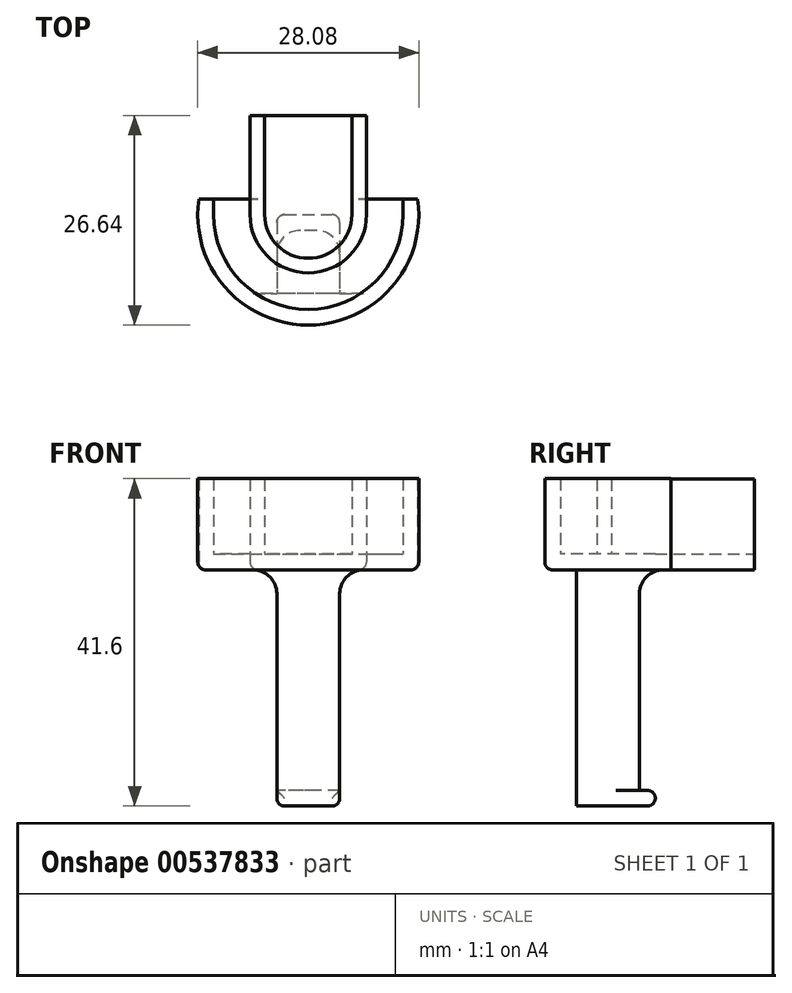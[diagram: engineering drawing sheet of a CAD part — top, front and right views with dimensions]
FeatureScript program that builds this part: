
annotation { "Feature Type Name" : "Feature", "Feature Type Description" : "" }
export const myFeature = defineFeature(function(context is Context, id is Id, definition is map)
    precondition{}
    {
        {
            var Q0;
            Q0=qCreatedBy(makeId("Top.planeOp"),FACE);
            var sketch = newSketch(context, id + "F0", { "sketchPlane" : qUnion([Q0])});
            skArc(sketch, "E0", {"start": v(-7.4, 0) * mm, "mid": v(0, -7.4) * mm, "end": v(7.4, 0) * mm});
            skLineSegment(sketch, "E1", {"start": v(-7.4, 0) * mm, "end": v(-7.4, 12.6) * mm});
            skLineSegment(sketch, "E2", {"start": v(7.4, 0) * mm, "end": v(7.4, 12.6) * mm});
            skLineSegment(sketch, "E3", {"start": v(7.4, 12.6) * mm, "end": v(-7.4, 12.6) * mm});
            skArc(sketch, "E4", {"start": v(-13.9, 2) * mm, "mid": v(0, -14.04) * mm, "end": v(13.9, 2) * mm});
            skLineSegment(sketch, "E5", {"start": v(-7.4, 2) * mm, "end": v(-13.9, 2) * mm});
            skLineSegment(sketch, "E6", {"start": v(7.4, 2) * mm, "end": v(13.9, 2) * mm});
            skSolve(sketch);
        }
        {
            var Q0;
            {var subQ1=sQuery(id+"F0.wireOp",EDGE,"E0");Q0=makeQuery(id+"F0.imprint","IMPRINT",FACE,{"disambiguationData":[TD([[makeQuery(id+"F0.imprint","IMPRINT",EDGE,{"derivedFrom":subQ1}),1.0]])]});}
            var Q1;
            {var subQ1=sQuery(id+"F0.wireOp",EDGE,"E0");Q1=makeQuery(id+"F0.imprint","IMPRINT",FACE,{"disambiguationData":[TD([[makeQuery(id+"F0.imprint","IMPRINT",EDGE,{"derivedFrom":subQ1}),-1.0]])]});}
            extrude(context, id + "F1", {"entities" : qUnion([Q0, Q1]), "depth" : 2 * mm});
        }
        {
            var Q0;
            Q0=makeQuery(id+"F1.opExtrude","CAP_FACE",FACE,{"disambiguationData":[OSD([sQuery(id+"F0.wireOp",EDGE,"E1"),sQuery(id+"F0.wireOp",EDGE,"E2"),sQuery(id+"F0.wireOp",EDGE,"E3"),sQuery(id+"F0.wireOp",EDGE,"E4"),sQuery(id+"F0.wireOp",EDGE,"E5"),sQuery(id+"F0.wireOp",EDGE,"E6")])],"isStart":false});
            var sketch = newSketch(context, id + "F2", { "sketchPlane" : qUnion([Q0])});
            skArc(sketch, "E7", {"start": v(-5.55, 0) * mm, "mid": v(0, -5.55) * mm, "end": v(5.55, 0) * mm});
            skLineSegment(sketch, "E8", {"start": v(-5.55, 0) * mm, "end": v(-5.55, 12.6) * mm});
            skLineSegment(sketch, "E9", {"start": v(5.55, 0) * mm, "end": v(5.55, 12.6) * mm});
            skArc(sketch, "E10", {"start": v(-7.4, 0) * mm, "mid": v(0, -7.4) * mm, "end": v(7.4, 0) * mm});
            skLineSegment(sketch, "E11", {"start": v(-7.4, 0) * mm, "end": v(-7.4, 12.6) * mm});
            skLineSegment(sketch, "E12", {"start": v(-7.4, 12.6) * mm, "end": v(-5.55, 12.6) * mm});
            skLineSegment(sketch, "E13", {"start": v(7.4, 0) * mm, "end": v(7.4, 12.6) * mm});
            skLineSegment(sketch, "E14", {"start": v(7.4, 12.6) * mm, "end": v(5.55, 12.6) * mm});
            skSolve(sketch);
        }
        {
            var Q0;
            Q0=makeQuery(id+"F2.imprint","IMPRINT",FACE,{"disambiguationData":[TD([[makeQuery(id+"F2.imprint","IMPRINT",EDGE,{"derivedFrom":sQuery(id+"F2.wireOp",EDGE,"E7")}),-1.0]])]});
            extrude(context, id + "F3", {"entities" : qUnion([Q0]), "operationType" : NewBodyOperationType.ADD, "depth" : 9.55 * mm});
        }
        {
            var Q0;
            {var subQ0=sQuery(id+"F0.wireOp",EDGE,"E5");var subQ1=sQuery(id+"F0.wireOp",EDGE,"E2");var subQ2=sQuery(id+"F0.wireOp",EDGE,"E4");var subQ3=sQuery(id+"F0.wireOp",EDGE,"E1");var subQ4=sQuery(id+"F0.wireOp",EDGE,"E6");Q0=makeQuery(id+"F3.boolean.opBoolean","SPLIT",FACE,{"disambiguationData":[TD([makeQuery(id+"F1.opExtrude","SWEPT_FACE",FACE,{"disambiguationData":[OSD([subQ3])]})])],"derivedFrom":makeQuery(id+"F1.opExtrude","CAP_FACE",FACE,{"disambiguationData":[OSD([subQ3,subQ1,sQuery(id+"F0.wireOp",EDGE,"E3"),subQ2,subQ0,subQ4])],"isStart":false})});}
            var sketch = newSketch(context, id + "F4", { "sketchPlane" : qUnion([Q0])});
            skArc(sketch, "E15", {"start": v(-12.04, 0) * mm, "mid": v(0, -12.04) * mm, "end": v(12.04, 0) * mm});
            skLineSegment(sketch, "E16", {"start": v(-12.04, 0) * mm, "end": v(-12.04, 2) * mm});
            skLineSegment(sketch, "E17", {"start": v(-12.04, 2) * mm, "end": v(-13.9, 2) * mm});
            skLineSegment(sketch, "E18", {"start": v(12.04, 0) * mm, "end": v(12.04, 2) * mm});
            skLineSegment(sketch, "E19", {"start": v(12.04, 2) * mm, "end": v(13.9, 2) * mm});
            skArc(sketch, "E20", {"start": v(-13.9, 2) * mm, "mid": v(0, -14.04) * mm, "end": v(13.9, 2) * mm});
            skSolve(sketch);
        }
        {
            var Q0;
            Q0=makeQuery(id+"F4.imprint","IMPRINT",FACE,{"disambiguationData":[TD([[makeQuery(id+"F4.imprint","IMPRINT",EDGE,{"derivedFrom":sQuery(id+"F4.wireOp",EDGE,"E15")}),-1.0]])]});
            extrude(context, id + "F5", {"entities" : qUnion([Q0]), "operationType" : NewBodyOperationType.ADD, "depth" : 9.6 * mm, "offsetDistance" : 25 * mm});
        }
        {
            var Q0;
            {var subQ1=sQuery(id+"F0.wireOp",EDGE,"E0");Q0=makeQuery(id+"F0.imprint","IMPRINT",FACE,{"disambiguationData":[TD([[makeQuery(id+"F0.imprint","IMPRINT",EDGE,{"derivedFrom":subQ1}),-1.0]])]});}
            var sketch = newSketch(context, id + "F6", { "sketchPlane" : qUnion([Q0])});
            skLineSegment(sketch, "E21.bottom", {"start": v(4, -2) * mm, "end": v(-4, -2) * mm});
            skLineSegment(sketch, "E21.top", {"start": v(4, -10) * mm, "end": v(-4, -10) * mm});
            skLineSegment(sketch, "E21.left", {"start": v(4, -2) * mm, "end": v(4, -10) * mm});
            skLineSegment(sketch, "E21.right", {"start": v(-4, -2) * mm, "end": v(-4, -10) * mm});
            skPoint(sketch, "E22.center.orphan", {"position": v(0, 0) * mm});
            skSolve(sketch);
        }
        {
            var Q0;
            Q0=makeQuery(id+"F1.opExtrude","CAP_EDGE",EDGE,{"disambiguationData":[OSD([sQuery(id+"F0.wireOp",EDGE,"E4")])],"isStart":true});
            var Q1;
            Q1=makeQuery(id+"F1.opExtrude","CAP_EDGE",EDGE,{"disambiguationData":[OSD([sQuery(id+"F0.wireOp",EDGE,"E1")])],"isStart":true});
            var Q2;
            Q2=makeQuery(id+"F1.opExtrude","CAP_EDGE",EDGE,{"disambiguationData":[OSD([sQuery(id+"F0.wireOp",EDGE,"E2")])],"isStart":true});
            fillet(context, id + "F7", {"entities" : qUnion([Q0, Q1, Q2]), "radius" : 1 * mm, "tangentPropagation" : true, "allowEdgeOverflow" : false});
        }
        {
            var Q0;
            Q0 = qSketchRegion(id + "F6", true);
            extrude(context, id + "F8", {"entities" : qUnion([Q0]), "operationType" : NewBodyOperationType.ADD, "oppositeDirection" : true, "depth" : 30 * mm, "offsetDistance" : 25 * mm});
        }
        {
            var Q0;
            Q0=makeQuery(id+"F8.opExtrude","SWEPT_FACE",FACE,{"disambiguationData":[OSD([sQuery(id+"F6.wireOp",EDGE,"E21.bottom")])]});
            var sketch = newSketch(context, id + "F9", { "sketchPlane" : qUnion([Q0])});
            skLineSegment(sketch, "E23.bottom", {"start": v(-4, -30) * mm, "end": v(4, -30) * mm});
            skLineSegment(sketch, "E23.top", {"start": v(-4, -28) * mm, "end": v(4, -28) * mm});
            skLineSegment(sketch, "E23.left", {"start": v(-4, -30) * mm, "end": v(-4, -28) * mm});
            skLineSegment(sketch, "E23.right", {"start": v(4, -30) * mm, "end": v(4, -28) * mm});
            skSolve(sketch);
        }
        {
            var Q0;
            Q0 = qSketchRegion(id + "F9", true);
            extrude(context, id + "F10", {"entities" : qUnion([Q0]), "operationType" : NewBodyOperationType.ADD, "depth" : 2 * mm, "offsetDistance" : 25 * mm});
        }
        {
            var Q0;
            Q0=makeQuery(id+"F8.opExtrude","SWEPT_EDGE",EDGE,{"disambiguationData":[OSD([sQuery(id+"F6.wireOp",EDGE,"E21.bottom"),sQuery(id+"F6.wireOp",EDGE,"E21.right")])]});
            var Q1;
            Q1=makeQuery(id+"F8.opExtrude","SWEPT_EDGE",EDGE,{"disambiguationData":[OSD([sQuery(id+"F6.wireOp",EDGE,"E21.bottom"),sQuery(id+"F6.wireOp",EDGE,"E21.left")])]});
            fillet(context, id + "F11", {"entities" : qUnion([Q0, Q1]), "radius" : 3 * mm, "tangentPropagation" : true, "allowEdgeOverflow" : false});
        }
        {
            var Q0;
            Q0=makeQuery(id+"F10.opExtrude","CAP_EDGE",EDGE,{"disambiguationData":[OSD([sQuery(id+"F9.wireOp",EDGE,"E23.top")])],"isStart":true});
            var Q1;
            Q1=makeQuery(id+"F10.opExtrude","CAP_EDGE",EDGE,{"disambiguationData":[OSD([sQuery(id+"F9.wireOp",EDGE,"E23.top")])],"isStart":false});
            var Q2;
            Q2=makeQuery(id+"F10.opExtrude","CAP_EDGE",EDGE,{"disambiguationData":[OSD([sQuery(id+"F9.wireOp",EDGE,"E23.bottom")])],"isStart":false});
            var Q3;
            Q3=makeQuery(id+"F10.opExtrude","CAP_EDGE",EDGE,{"disambiguationData":[OSD([sQuery(id+"F9.wireOp",EDGE,"E23.right")])],"isStart":false});
            var Q4;
            Q4=makeQuery(id+"F10.opExtrude","CAP_EDGE",EDGE,{"disambiguationData":[OSD([sQuery(id+"F9.wireOp",EDGE,"E23.left")])],"isStart":false});
            fillet(context, id + "F12", {"entities" : qUnion([Q0, Q1, Q2, Q3, Q4]), "radius" : 1 * mm, "tangentPropagation" : true, "allowEdgeOverflow" : false});
        }
        {
            var Q0;
            Q0=makeQuery(id+"F10.boolean.opBoolean","MERGE",EDGE,{"derivedFrom":[makeQuery(id+"F8.opExtrude","CAP_EDGE",EDGE,{"disambiguationData":[OSD([sQuery(id+"F6.wireOp",EDGE,"E21.left")])],"isStart":false}),makeQuery(id+"F10.opExtrude","SWEPT_EDGE",EDGE,{"disambiguationData":[OSD([sQuery(id+"F9.wireOp",EDGE,"E23.bottom"),sQuery(id+"F9.wireOp",EDGE,"E23.left")])]})]});
            var Q1;
            Q1=makeQuery(id+"F10.boolean.opBoolean","MERGE",EDGE,{"derivedFrom":[makeQuery(id+"F8.opExtrude","CAP_EDGE",EDGE,{"disambiguationData":[OSD([sQuery(id+"F6.wireOp",EDGE,"E21.right")])],"isStart":false}),makeQuery(id+"F10.opExtrude","SWEPT_EDGE",EDGE,{"disambiguationData":[OSD([sQuery(id+"F9.wireOp",EDGE,"E23.bottom"),sQuery(id+"F9.wireOp",EDGE,"E23.right")])]})]});
            fillet(context, id + "F13", {"entities" : qUnion([Q0, Q1]), "radius" : 1 * mm, "tangentPropagation" : true, "allowEdgeOverflow" : false});
        }
        {
            var Q0;
            Q0=makeQuery(id+"F11.opFillet","BLEND_EDGE",EDGE,{"blendedFrom":[makeQuery(id+"F8.opExtrude","SWEPT_EDGE",EDGE,{"disambiguationData":[OSD([sQuery(id+"F6.wireOp",EDGE,"E21.bottom"),sQuery(id+"F6.wireOp",EDGE,"E21.left")])]}),makeQuery(id+"F1.opExtrude","CAP_FACE",FACE,{"disambiguationData":[OSD([sQuery(id+"F0.wireOp",EDGE,"E1"),sQuery(id+"F0.wireOp",EDGE,"E2"),sQuery(id+"F0.wireOp",EDGE,"E3"),sQuery(id+"F0.wireOp",EDGE,"E4"),sQuery(id+"F0.wireOp",EDGE,"E5"),sQuery(id+"F0.wireOp",EDGE,"E6")])],"isStart":true})],"blendedInto":[makeQuery(id+"F1.opExtrude","CAP_FACE",FACE,{"disambiguationData":[OSD([sQuery(id+"F0.wireOp",EDGE,"E1"),sQuery(id+"F0.wireOp",EDGE,"E2"),sQuery(id+"F0.wireOp",EDGE,"E3"),sQuery(id+"F0.wireOp",EDGE,"E4"),sQuery(id+"F0.wireOp",EDGE,"E5"),sQuery(id+"F0.wireOp",EDGE,"E6")])],"isStart":true})]});
            var Q1;
            Q1=makeQuery(id+"F8.opExtrude","CAP_EDGE",EDGE,{"disambiguationData":[OSD([sQuery(id+"F6.wireOp",EDGE,"E21.bottom")])],"isStart":true});
            var Q2;
            Q2=makeQuery(id+"F11.opFillet","BLEND_EDGE",EDGE,{"blendedFrom":[makeQuery(id+"F8.opExtrude","SWEPT_EDGE",EDGE,{"disambiguationData":[OSD([sQuery(id+"F6.wireOp",EDGE,"E21.bottom"),sQuery(id+"F6.wireOp",EDGE,"E21.right")])]}),makeQuery(id+"F1.opExtrude","CAP_FACE",FACE,{"disambiguationData":[OSD([sQuery(id+"F0.wireOp",EDGE,"E1"),sQuery(id+"F0.wireOp",EDGE,"E2"),sQuery(id+"F0.wireOp",EDGE,"E3"),sQuery(id+"F0.wireOp",EDGE,"E4"),sQuery(id+"F0.wireOp",EDGE,"E5"),sQuery(id+"F0.wireOp",EDGE,"E6")])],"isStart":true})],"blendedInto":[makeQuery(id+"F1.opExtrude","CAP_FACE",FACE,{"disambiguationData":[OSD([sQuery(id+"F0.wireOp",EDGE,"E1"),sQuery(id+"F0.wireOp",EDGE,"E2"),sQuery(id+"F0.wireOp",EDGE,"E3"),sQuery(id+"F0.wireOp",EDGE,"E4"),sQuery(id+"F0.wireOp",EDGE,"E5"),sQuery(id+"F0.wireOp",EDGE,"E6")])],"isStart":true})]});
            fillet(context, id + "F14", {"entities" : qUnion([Q0, Q1, Q2]), "radius" : 3 * mm, "tangentPropagation" : true, "allowEdgeOverflow" : false});
        }
    });
